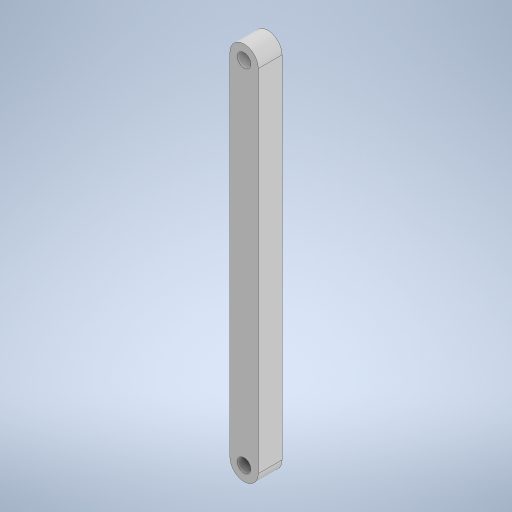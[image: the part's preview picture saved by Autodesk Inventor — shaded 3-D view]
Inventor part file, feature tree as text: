
AUTODESK INVENTOR PART (.ipt)
format: ipt  version: 2023 (Build 270158000, 158)  size: 242,688 bytes
history: native  units: mm
features: extrude x1, sketch x1
ambient origin geometry x8: Origin, YZ Plane, XZ Plane, XY Plane, X Axis, Y Axis, Z Axis, Center Point
bodies: Solid1 (feature_tree)
feature tree (2):
  extrude  "Extrusion1"  Depth=6.0mm
  sketch  "Sketch1"  dims[d8=5.0mm d9=0.0mm d10=6.0mm d11=80.0mm d12=3.0mm d13=6.0mm d14=2.85mm d15=3.0mm d16=6.0mm d17=2.85mm]
